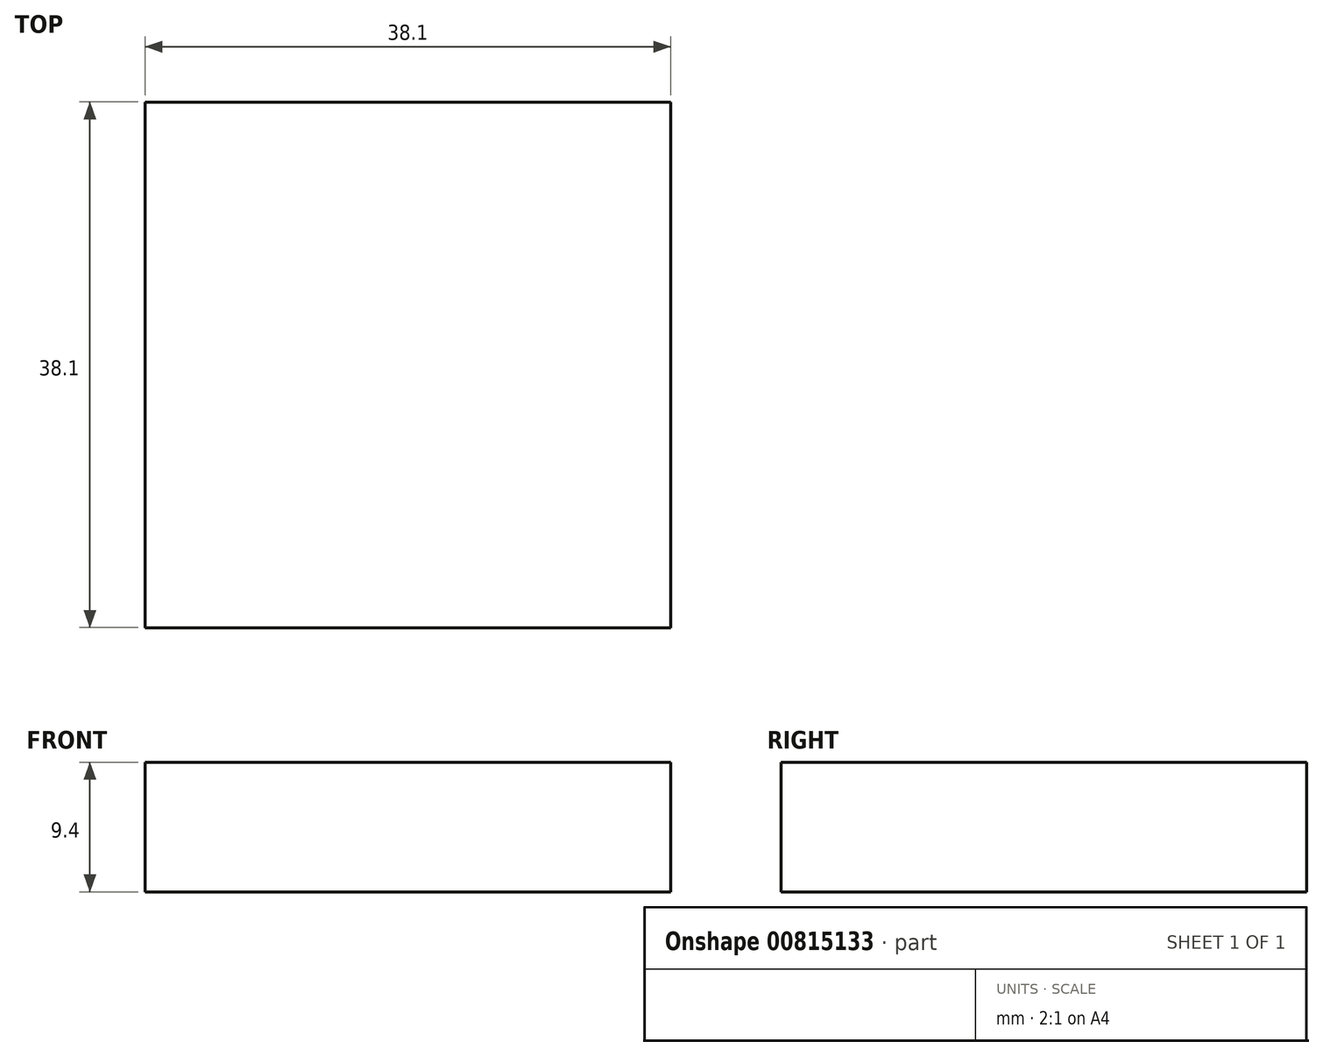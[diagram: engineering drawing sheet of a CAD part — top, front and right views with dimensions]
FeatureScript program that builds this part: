
annotation { "Feature Type Name" : "Feature", "Feature Type Description" : "" }
export const myFeature = defineFeature(function(context is Context, id is Id, definition is map)
    precondition{}
    {
        {
            var Q0;
            Q0=qCreatedBy(makeId("Top.planeOp"),FACE);
            var sketch = newSketch(context, id + "F0", { "sketchPlane" : qUnion([Q0])});
            skLineSegment(sketch, "E0.bottom", {"start": v(-20.63, 20.25) * mm, "end": v(17.47, 20.25) * mm});
            skLineSegment(sketch, "E0.top", {"start": v(-20.63, -17.85) * mm, "end": v(17.47, -17.85) * mm});
            skLineSegment(sketch, "E0.left", {"start": v(-20.63, 20.25) * mm, "end": v(-20.63, -17.85) * mm});
            skLineSegment(sketch, "E0.right", {"start": v(17.47, 20.25) * mm, "end": v(17.47, -17.85) * mm});
            skSolve(sketch);
        }
        {
            var Q0;
            Q0 = qSketchRegion(id + "F0", true);
            extrude(context, id + "F1", {"entities" : qUnion([Q0]), "depth" : 9.4 * mm, "offsetDistance" : 25.4 * mm});
        }
    });
